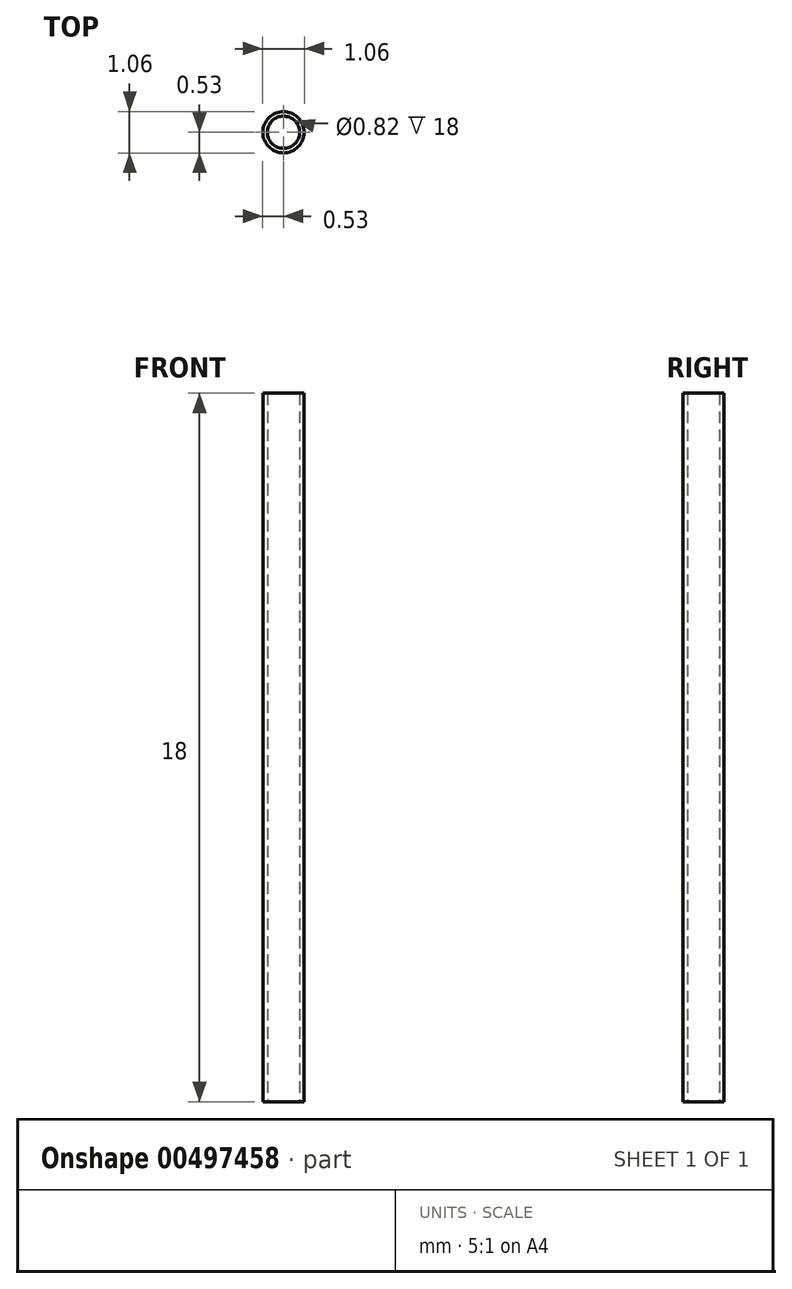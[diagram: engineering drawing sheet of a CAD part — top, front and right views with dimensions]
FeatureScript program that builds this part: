
annotation { "Feature Type Name" : "Feature", "Feature Type Description" : "" }
export const myFeature = defineFeature(function(context is Context, id is Id, definition is map)
    precondition{}
    {
        {
            var Q0;
            Q0=qCreatedBy(makeId("Top.planeOp"),FACE);
            var sketch = newSketch(context, id + "F0", { "sketchPlane" : qUnion([Q0])});
            skCircle(sketch, "E0", {"center": v(0, 0) * mm, "radius": 0.41 * mm});
            skCircle(sketch, "E1", {"center": v(0, 0) * mm, "radius": 0.53 * mm});
            skSolve(sketch);
        }
        {
            var Q0;
            Q0=makeQuery(id+"F0.imprint","IMPRINT",FACE,{"disambiguationData":[TD([[makeQuery(id+"F0.imprint","IMPRINT",EDGE,{"derivedFrom":sQuery(id+"F0.wireOp",EDGE,"E0")}),-1.0]])]});
            extrude(context, id + "F1", {"entities" : qUnion([Q0]), "depth" : 18 * mm});
        }
    });
